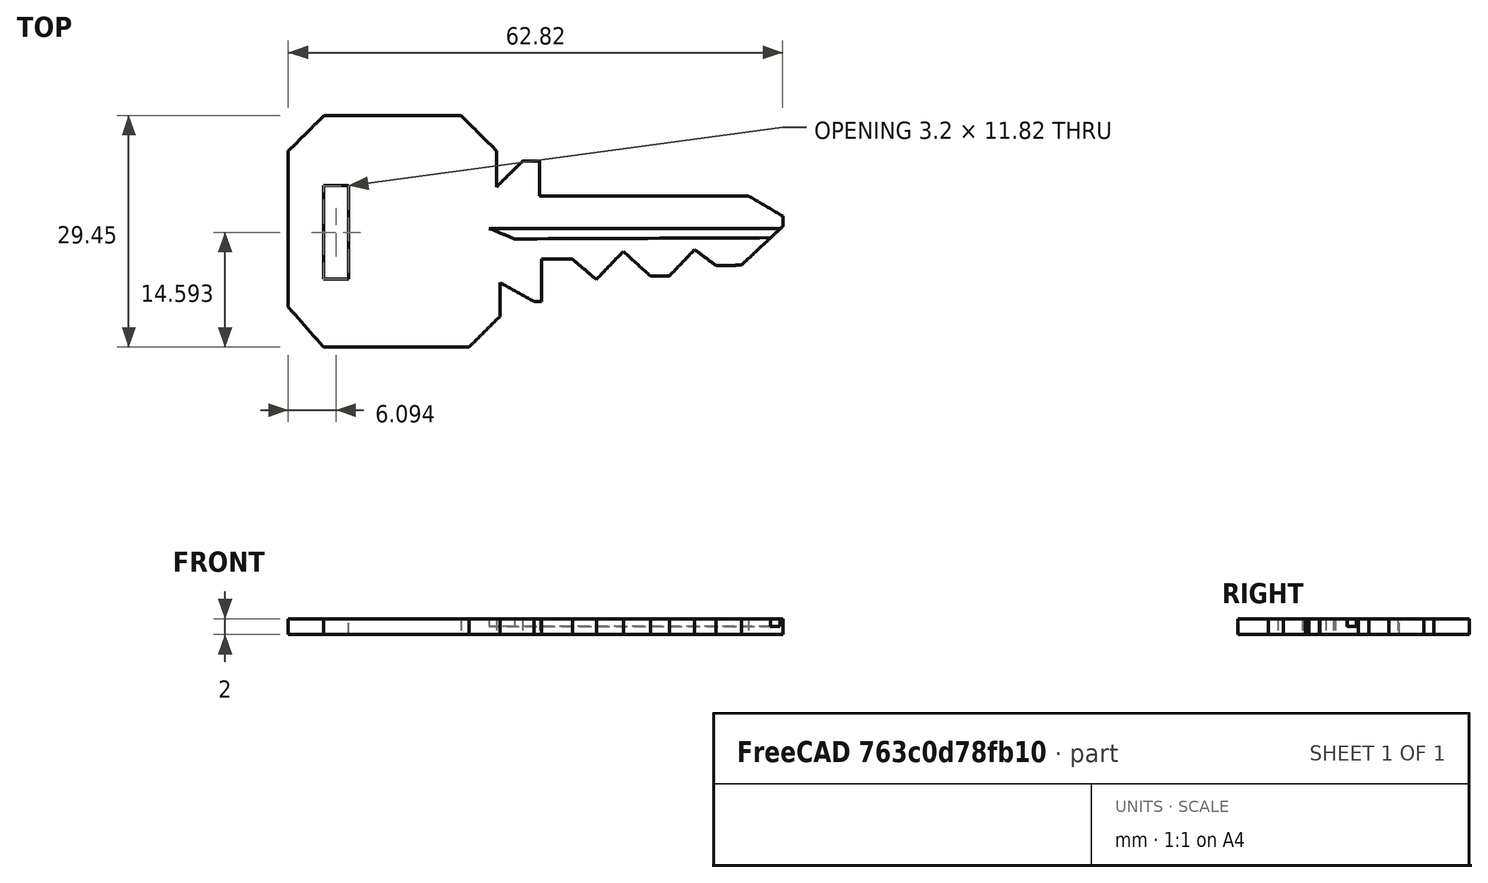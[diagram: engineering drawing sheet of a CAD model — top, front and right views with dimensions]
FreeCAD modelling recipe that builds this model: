
FCSTD DOCUMENT  (FreeCAD 0.17R13217 (Git))
Label: 01-llave
License: All rights reserved
LicenseURL: http://en.wikipedia.org/wiki/All_rights_reserved
objects: Part::Feature×3, Part::Extrusion×3, Part::Cut×2
note: 8 computed .brp shape members not serialized (recipe doc carries the construction recipe); baked Part::Feature solids carry a one-line shape summary decoded from their .brp

FEATURE [Part::Feature] path4167  label="Contorno-llave"
  shape: bbox 62.82 x 29.44 x 2e-07 mm, 0 faces, 0 solids (baked)
FEATURE [Part::Feature] path4171  label="contorno-taladro"
  shape: bbox 3.198 x 11.82 x 2e-07 mm, 0 faces, 0 solids (baked)
FEATURE [Part::Feature] path4175  label="contorno-muesca"
  shape: bbox 40.36 x 1.34 x 2e-07 mm, 0 faces, 0 solids (baked)
FEATURE [Part::Extrusion] Extrude  label="base-llave"
  Base = -> path4167
  Dir = (0,0,-1)
  DirMode = 2
  FaceMakerClass = Part::FaceMakerBullseye
  LengthFwd = 2
  LengthRev = 0
  Solid = true
  Symmetric = false
FEATURE [Part::Extrusion] Extrude001  label="muesca"
  Base = -> path4175
  Dir = (0,0,-1)
  DirMode = 2
  FaceMakerClass = Part::FaceMakerBullseye
  LengthFwd = 2
  LengthRev = 0
  Placement = pos=(0,0,1) rot=(0,0,1;0rad)
  Solid = true
  Symmetric = false
FEATURE [Part::Extrusion] Extrude002  label="taladro-llave"
  Base = -> path4171
  Dir = (0,0,1)
  DirMode = 2
  FaceMakerClass = Part::FaceMakerBullseye
  LengthFwd = 5
  LengthRev = 0
  Placement = pos=(0,0,-3) rot=(0,0,1;0rad)
  Solid = true
  Symmetric = false
FEATURE [Part::Cut] Cut
  Base = -> Extrude
  Refine = true
  Tool = -> Extrude001
FEATURE [Part::Cut] Cut001  label="Llave-final"
  Base = -> Cut
  Refine = true
  Tool = -> Extrude002
